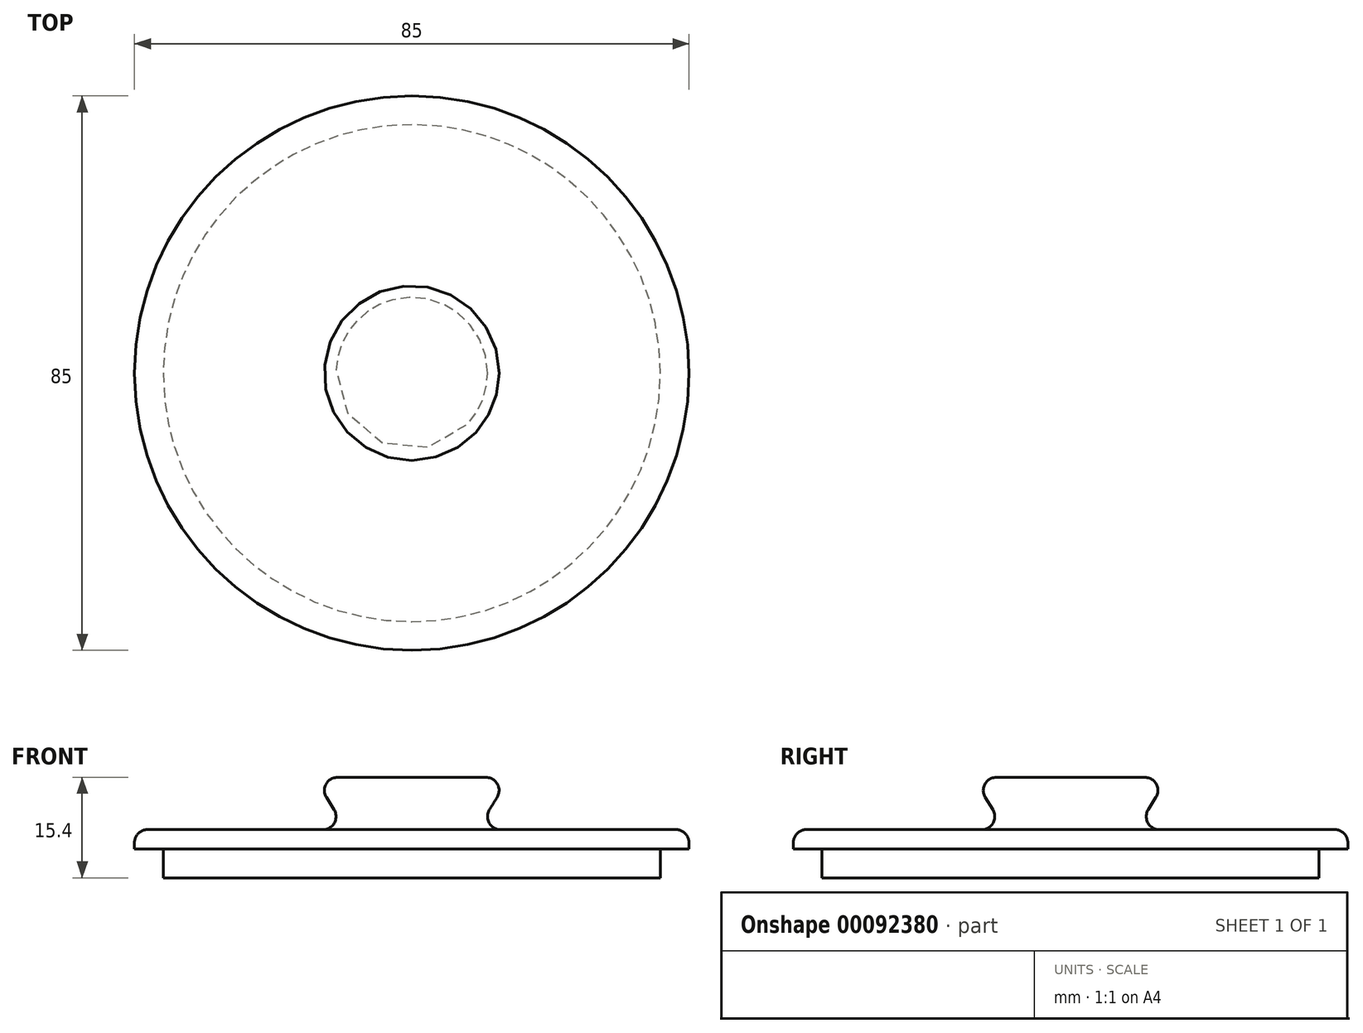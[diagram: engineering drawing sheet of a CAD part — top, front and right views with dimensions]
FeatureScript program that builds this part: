
annotation { "Feature Type Name" : "Feature", "Feature Type Description" : "" }
export const myFeature = defineFeature(function(context is Context, id is Id, definition is map)
    precondition{}
    {
        {
            var Q0;
            Q0=qCreatedBy(makeId("Front.planeOp"),FACE);
            var sketch = newSketch(context, id + "F0", { "sketchPlane" : qUnion([Q0])});
            skLineSegment(sketch, "E0", {"start": v(38.1, 0) * mm, "end": v(38.1, 4.4) * mm});
            skLineSegment(sketch, "E1", {"start": v(38.1, 4.4) * mm, "end": v(42.5, 4.4) * mm});
            skLineSegment(sketch, "E2", {"start": v(42.5, 4.4) * mm, "end": v(42.5, 5.4) * mm});
            skLineSegment(sketch, "E3", {"start": v(0, 0) * mm, "end": v(38.1, 0) * mm});
            skLineSegment(sketch, "E4", {"start": v(0, 69.98) * mm, "end": v(0, -47.1) * mm, "construction": true});
            skLineSegment(sketch, "E5", {"start": v(0, 15.4) * mm, "end": v(0, 0) * mm});
            skLineSegment(sketch, "E6", {"start": v(40.5, 7.4) * mm, "end": v(13.6, 7.4) * mm});
            skLineSegment(sketch, "E7", {"start": v(11.91, 10.46) * mm, "end": v(13.09, 12.34) * mm});
            skLineSegment(sketch, "E8", {"start": v(11.4, 15.4) * mm, "end": v(0, 15.4) * mm});
            skPoint(sketch, "E9.visualSharp", {"position": v(15, 15.4) * mm});
            skArc(sketch, "E9.filletArc", {"start": v(13.09, 12.34) * mm, "mid": v(13.14, 14.37) * mm, "end": v(11.4, 15.4) * mm});
            skPoint(sketch, "E10.visualSharp", {"position": v(10, 7.4) * mm});
            skArc(sketch, "E10.filletArc", {"start": v(11.91, 10.46) * mm, "mid": v(11.86, 8.43) * mm, "end": v(13.6, 7.4) * mm});
            skPoint(sketch, "E11.visualSharp", {"position": v(42.5, 7.4) * mm});
            skArc(sketch, "E11.filletArc", {"start": v(42.5, 5.4) * mm, "mid": v(41.91, 6.81) * mm, "end": v(40.5, 7.4) * mm});
            skSolve(sketch);
        }
        {
            var Q0;
            Q0=makeQuery(id+"F0.imprint","IMPRINT",FACE,{"disambiguationData":[TD([[makeQuery(id+"F0.imprint","IMPRINT",EDGE,{"derivedFrom":sQuery(id+"F0.wireOp",EDGE,"E0")}),1.0]])]});
            var Q1;
            Q1=sQuery(id+"F0.wireOp",EDGE,"E4");
            revolve(context, id + "F1", {"entities" : qUnion([Q0]), "axis" : qUnion([Q1]), "revolveType" : RevolveType.FULL});
        }
    });
